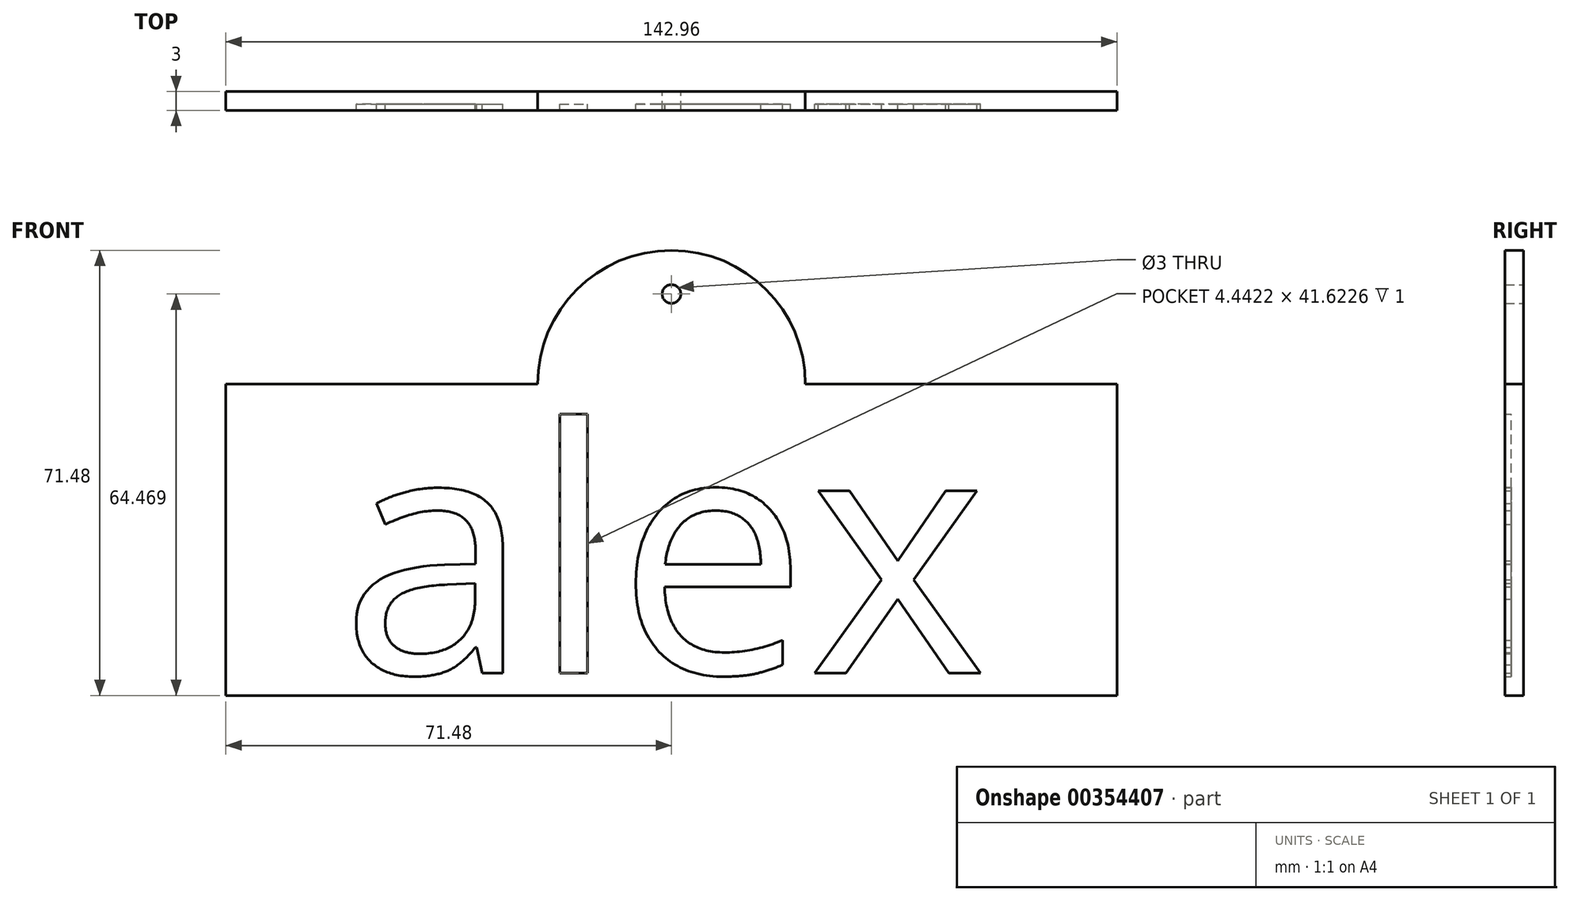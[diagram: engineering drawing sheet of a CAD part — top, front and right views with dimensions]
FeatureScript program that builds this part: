
annotation { "Feature Type Name" : "Feature", "Feature Type Description" : "" }
export const myFeature = defineFeature(function(context is Context, id is Id, definition is map)
    precondition{}
    {
        {
            var Q0;
            Q0=qCreatedBy(makeId("Front.planeOp"),FACE);
            var sketch = newSketch(context, id + "F0", { "sketchPlane" : qUnion([Q0])});
            skLineSegment(sketch, "E0.bottom", {"start": v(71.48, -25) * mm, "end": v(-71.48, -25) * mm});
            skLineSegment(sketch, "E0.top", {"start": v(71.48, 25) * mm, "end": v(21.48, 25) * mm});
            skLineSegment(sketch, "E0.left", {"start": v(71.48, -25) * mm, "end": v(71.48, 25) * mm});
            skLineSegment(sketch, "E0.right", {"start": v(-71.48, -25) * mm, "end": v(-71.48, 25) * mm});
            skPoint(sketch, "E0.middle", {"position": v(0, 0) * mm});
            skArc(sketch, "E1", {"start": v(21.48, 25) * mm, "mid": v(0, 46.48) * mm, "end": v(-21.48, 25) * mm});
            skCircle(sketch, "E2", {"center": v(0, 39.47) * mm, "radius": 1.5 * mm});
            skLineSegment(sketch, "E3.trimOffspring", {"start": v(-21.48, 25) * mm, "end": v(-71.48, 25) * mm});
            skText(sketch, "E4", { "text": "alex\n", "fontName": "OpenSans-Regular.ttf"});
            const initialGuessF0  = {"E4": [-0.0531, -0.02144, 1, 0, 0.03944]};
            skSetInitialGuess(sketch, initialGuessF0);
            skSolve(sketch);
        }
        {
            var Q0;
            Q0=makeQuery(id+"F0.imprint","IMPRINT",FACE,{"disambiguationData":[TD([[makeQuery(id+"F0.imprint","IMPRINT",EDGE,{"derivedFrom":sQuery(id+"F0.wireOp",EDGE,"E4.sketch_text.stroke-19")}),1.0]])]});
            var Q1;
            Q1=makeQuery(id+"F0.imprint","IMPRINT",FACE,{"disambiguationData":[TD([[makeQuery(id+"F0.imprint","IMPRINT",EDGE,{"derivedFrom":sQuery(id+"F0.wireOp",EDGE,"E4.sketch_text.stroke-27")}),-1.0]])]});
            var Q2;
            Q2=makeQuery(id+"F0.imprint","IMPRINT",FACE,{"disambiguationData":[TD([[makeQuery(id+"F0.imprint","IMPRINT",EDGE,{"derivedFrom":sQuery(id+"F0.wireOp",EDGE,"E4.sketch_text.stroke-45")}),1.0]])]});
            var Q3;
            Q3=makeQuery(id+"F0.imprint","IMPRINT",FACE,{"disambiguationData":[TD([[makeQuery(id+"F0.imprint","IMPRINT",EDGE,{"derivedFrom":sQuery(id+"F0.wireOp",EDGE,"E4.sketch_text.stroke-50")}),-1.0]])]});
            var Q4;
            Q4=makeQuery(id+"F0.imprint","IMPRINT",FACE,{"disambiguationData":[TD([[makeQuery(id+"F0.imprint","IMPRINT",EDGE,{"derivedFrom":sQuery(id+"F0.wireOp",EDGE,"E4.sketch_text.stroke-0")}),-1.0]])]});
            var Q5;
            Q5=makeQuery(id+"F0.imprint","IMPRINT",FACE,{"disambiguationData":[TD([[makeQuery(id+"F0.imprint","IMPRINT",EDGE,{"derivedFrom":sQuery(id+"F0.wireOp",EDGE,"E4.sketch_text.stroke-31")}),-1.0]])]});
            var Q6;
            Q6=makeQuery(id+"F0.imprint","IMPRINT",FACE,{"disambiguationData":[TD([[makeQuery(id+"F0.imprint","IMPRINT",EDGE,{"derivedFrom":sQuery(id+"F0.wireOp",EDGE,"E0.bottom")}),-1.0]])]});
            extrude(context, id + "F1", {"entities" : qUnion([Q0, Q1, Q2, Q3, Q4, Q5, Q6]), "depth" : 2 * mm});
        }
        {
            var Q0;
            Q0=makeQuery(id+"F0.imprint","IMPRINT",FACE,{"disambiguationData":[TD([[makeQuery(id+"F0.imprint","IMPRINT",EDGE,{"derivedFrom":sQuery(id+"F0.wireOp",EDGE,"E0.bottom")}),-1.0]])]});
            var Q1;
            Q1=makeQuery(id+"F0.imprint","IMPRINT",FACE,{"disambiguationData":[TD([[makeQuery(id+"F0.imprint","IMPRINT",EDGE,{"derivedFrom":sQuery(id+"F0.wireOp",EDGE,"E4.sketch_text.stroke-45")}),1.0]])]});
            var Q2;
            Q2=makeQuery(id+"F0.imprint","IMPRINT",FACE,{"disambiguationData":[TD([[makeQuery(id+"F0.imprint","IMPRINT",EDGE,{"derivedFrom":sQuery(id+"F0.wireOp",EDGE,"E4.sketch_text.stroke-19")}),1.0]])]});
            extrude(context, id + "F2", {"entities" : qUnion([Q0, Q1, Q2]), "operationType" : NewBodyOperationType.ADD, "depth" : 3 * mm});
        }
    });
